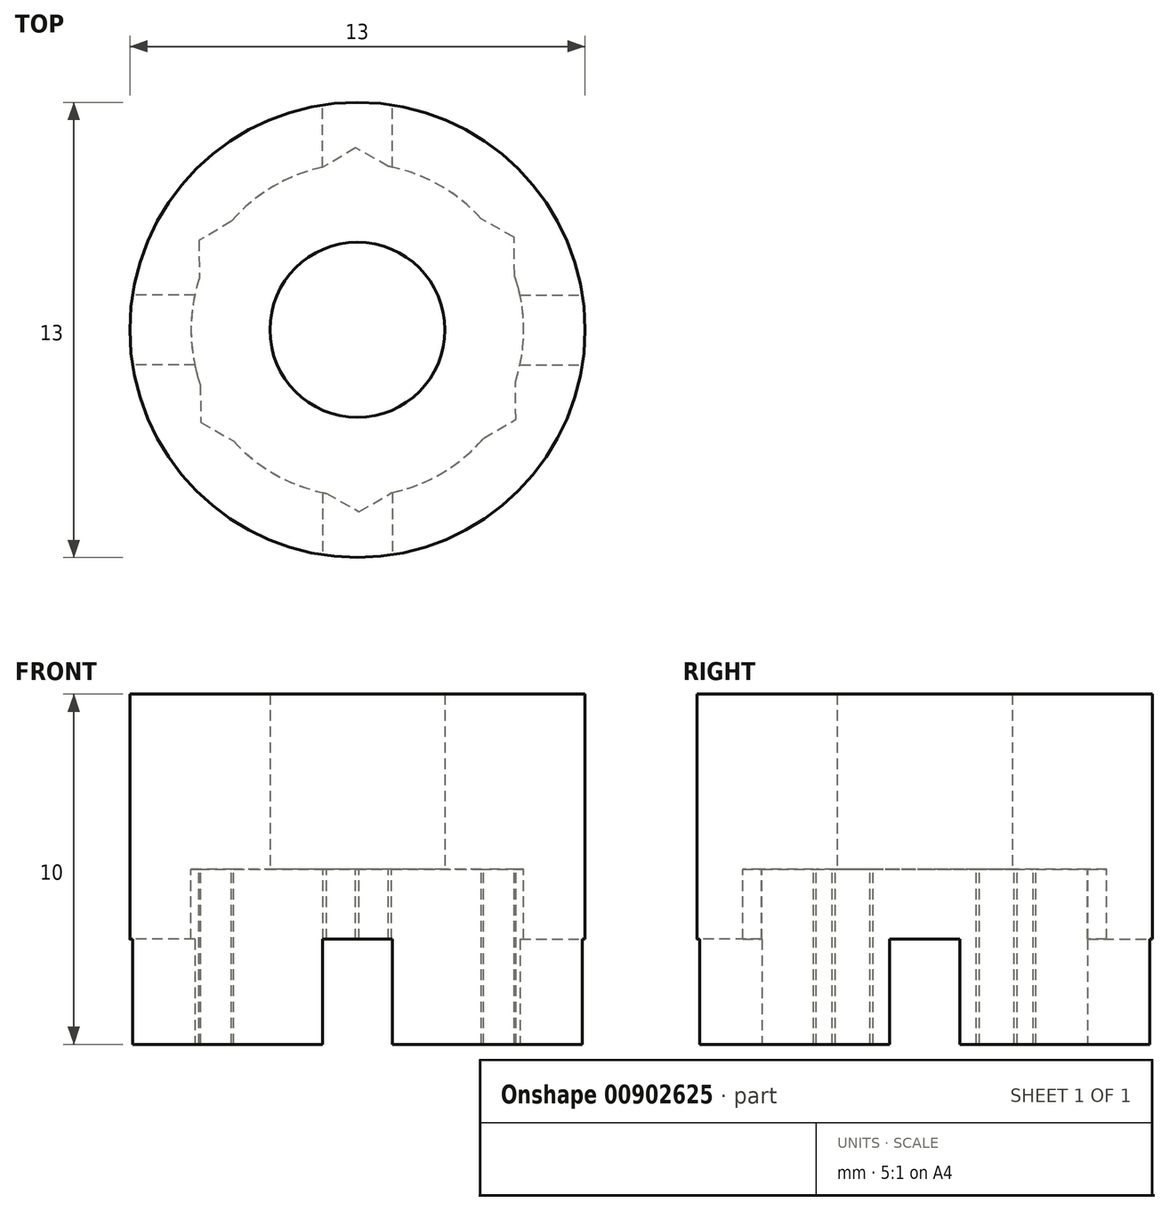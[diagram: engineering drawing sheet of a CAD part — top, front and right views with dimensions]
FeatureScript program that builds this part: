
annotation { "Feature Type Name" : "Feature", "Feature Type Description" : "" }
export const myFeature = defineFeature(function(context is Context, id is Id, definition is map)
    precondition{}
    {
        {
            var Q0;
            Q0=qCreatedBy(makeId("Top.planeOp"),FACE);
            var sketch = newSketch(context, id + "F0", { "sketchPlane" : qUnion([Q0])});
            skCircle(sketch, "E0", {"center": v(0, 0) * mm, "radius": 6.5 * mm});
            skCircle(sketch, "E1", {"center": v(0, 0) * mm, "radius": 2.5 * mm});
            skCircle(sketch, "E2", {"center": v(0, 0) * mm, "radius": 4.75 * mm});
            skSolve(sketch);
        }
        {
            var Q0;
            Q0=makeQuery(id+"F0.imprint","IMPRINT",FACE,{"disambiguationData":[TD([[makeQuery(id+"F0.imprint","IMPRINT",EDGE,{"derivedFrom":sQuery(id+"F0.wireOp",EDGE,"E0")}),1.0]])]});
            extrude(context, id + "F1", {"entities" : qUnion([Q0]), "oppositeDirection" : true, "depth" : 5 * mm, "offsetDistance" : 25 * mm});
        }
        {
            var Q0;
            Q0=makeQuery(id+"F0.imprint","IMPRINT",FACE,{"disambiguationData":[TD([[makeQuery(id+"F0.imprint","IMPRINT",EDGE,{"derivedFrom":sQuery(id+"F0.wireOp",EDGE,"E1")}),-1.0]])]});
            var Q1;
            Q1=makeQuery(id+"F0.imprint","IMPRINT",FACE,{"disambiguationData":[TD([[makeQuery(id+"F0.imprint","IMPRINT",EDGE,{"derivedFrom":sQuery(id+"F0.wireOp",EDGE,"E0")}),1.0]])]});
            extrude(context, id + "F2", {"entities" : qUnion([Q0, Q1]), "operationType" : NewBodyOperationType.ADD, "depth" : 5 * mm, "offsetDistance" : 25 * mm});
        }
        {
            var Q0;
            Q0=makeQuery(id+"F1.opExtrude","CAP_FACE",FACE,{"disambiguationData":[OSD([sQuery(id+"F0.wireOp",EDGE,"E0"),sQuery(id+"F0.wireOp",EDGE,"E2")])],"isStart":false});
            var sketch = newSketch(context, id + "F3", { "sketchPlane" : qUnion([Q0])});
            skLineSegment(sketch, "E3.bottom", {"start": v(-4.64, 1) * mm, "end": v(-6.5, 1) * mm});
            skLineSegment(sketch, "E3.top", {"start": v(-4.64, -1) * mm, "end": v(-6.5, -1) * mm});
            skLineSegment(sketch, "E3.left", {"start": v(-4.64, 1) * mm, "end": v(-4.64, -1) * mm});
            skLineSegment(sketch, "E3.right", {"start": v(-6.5, 1) * mm, "end": v(-6.5, -1) * mm});
            skPoint(sketch, "E3.middle", {"position": v(-5.57, 0) * mm});
            skPoint(sketch, "E4", {"position": v(-6.5, 0) * mm});
            skLineSegment(sketch, "E5.1.0", {"start": v(-1, -4.64) * mm, "end": v(1, -4.64) * mm});
            skLineSegment(sketch, "E5.1.1", {"start": v(-1, -6.5) * mm, "end": v(1, -6.5) * mm});
            skPoint(sketch, "E5.1.2", {"position": v(0, -5.57) * mm});
            skPoint(sketch, "E5.1.3", {"position": v(0, -6.5) * mm});
            skLineSegment(sketch, "E5.1.4", {"start": v(-1, -4.64) * mm, "end": v(-1, -6.5) * mm});
            skLineSegment(sketch, "E5.1.5", {"start": v(1, -4.64) * mm, "end": v(1, -6.5) * mm});
            skLineSegment(sketch, "E5.2.0", {"start": v(4.64, -1) * mm, "end": v(4.64, 1) * mm});
            skLineSegment(sketch, "E5.2.1", {"start": v(6.5, -1) * mm, "end": v(6.5, 1) * mm});
            skPoint(sketch, "E5.2.2", {"position": v(5.57, 0) * mm});
            skPoint(sketch, "E5.2.3", {"position": v(6.5, 0) * mm});
            skLineSegment(sketch, "E5.2.4", {"start": v(4.64, -1) * mm, "end": v(6.5, -1) * mm});
            skLineSegment(sketch, "E5.2.5", {"start": v(4.64, 1) * mm, "end": v(6.5, 1) * mm});
            skLineSegment(sketch, "E5.3.0", {"start": v(1, 4.64) * mm, "end": v(-1, 4.64) * mm});
            skLineSegment(sketch, "E5.3.1", {"start": v(1, 6.5) * mm, "end": v(-1, 6.5) * mm});
            skPoint(sketch, "E5.3.2", {"position": v(0, 5.57) * mm});
            skPoint(sketch, "E5.3.3", {"position": v(0, 6.5) * mm});
            skLineSegment(sketch, "E5.3.4", {"start": v(1, 4.64) * mm, "end": v(1, 6.5) * mm});
            skLineSegment(sketch, "E5.3.5", {"start": v(-1, 4.64) * mm, "end": v(-1, 6.5) * mm});
            skPoint(sketch, "E5.center", {"position": v(0, 0) * mm});
            skSolve(sketch);
        }
        {
            var Q0;
            Q0 = qSketchRegion(id + "F3", true);
            extrude(context, id + "F4", {"entities" : qUnion([Q0]), "operationType" : NewBodyOperationType.REMOVE, "oppositeDirection" : true, "depth" : 3 * mm, "offsetDistance" : 25 * mm});
        }
        {
            var Q0;
            Q0=makeQuery(id+"F0.imprint","IMPRINT",FACE,{"disambiguationData":[TD([[makeQuery(id+"F0.imprint","IMPRINT",EDGE,{"derivedFrom":sQuery(id+"F0.wireOp",EDGE,"E1")}),-1.0]])]});
            var sketch = newSketch(context, id + "F5", { "sketchPlane" : qUnion([Q0])});
            skCircle(sketch, "E6.cCircle", {"center": v(0, 0) * mm, "radius": 4.5 * mm, "construction": true});
            skLineSegment(sketch, "E6.0", {"start": v(4.53, -2.55) * mm, "end": v(0.05, -5.2) * mm});
            skLineSegment(sketch, "E6.1", {"start": v(0.05, -5.2) * mm, "end": v(-4.47, -2.64) * mm});
            skLineSegment(sketch, "E6.2", {"start": v(-4.47, -2.64) * mm, "end": v(-4.53, 2.55) * mm});
            skLineSegment(sketch, "E6.3", {"start": v(-4.53, 2.55) * mm, "end": v(-0.05, 5.2) * mm});
            skLineSegment(sketch, "E6.4", {"start": v(-0.05, 5.2) * mm, "end": v(4.47, 2.64) * mm});
            skLineSegment(sketch, "E6.5", {"start": v(4.47, 2.64) * mm, "end": v(4.53, -2.55) * mm});
            skPoint(sketch, "E6.0.midPoint", {"position": v(2.29, -3.87) * mm});
            skSolve(sketch);
        }
        {
            var Q0;
            Q0 = qSketchRegion(id + "F5", true);
            var Q1;
            {var subQ0=sQuery(id+"F0.wireOp",EDGE,"E0");var subQ1=sQuery(id+"F0.wireOp",EDGE,"E2");Q1=makeQuery(id+"F4.boolean.opBoolean","SPLIT",FACE,{"disambiguationData":[TD([makeQuery(id+"F4.opExtrude","SWEPT_FACE",FACE,{"disambiguationData":[OSD([sQuery(id+"F3.wireOp",EDGE,"E3.bottom")])]})])],"derivedFrom":makeQuery(id+"F1.opExtrude","CAP_FACE",FACE,{"disambiguationData":[OSD([subQ0,subQ1])],"isStart":false})});}
            extrude(context, id + "F6", {"entities" : qUnion([Q0]), "operationType" : NewBodyOperationType.REMOVE, "endBound" : BoundingType.UP_TO_SURFACE, "oppositeDirection" : true, "depth" : 25 * mm, "endBoundEntityFace" : qUnion([Q1]), "offsetDistance" : 25 * mm});
        }
    });
